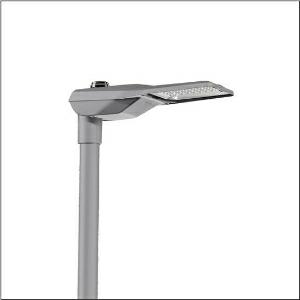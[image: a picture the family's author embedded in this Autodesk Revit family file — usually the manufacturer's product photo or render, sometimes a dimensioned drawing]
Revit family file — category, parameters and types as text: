
# Revit family: streetlight_sl_21_mini___st0_5a_5xe6b37n08hb_16a2
name_source: partatom
category: Lighting Fixtures
units: mm (PartAtom-declared; Revit-internal decimal feet)

## family parameters
Cut with Voids When Loaded = No
Host = Face
Light Source = No
Part Type = Normal
Room Calculation Point = No
Round Connector Dimension = Use Diameter
Shared = No

## types (1)
- --- (1 x LED, 9040 lm, 66 W, 3000K)
    Apparent Load = 66 VA
    CIE Flux Codes = 41 75 97 100 100
    Color Rendering = 70
    Color Temperature = 3000K
    Default Elevation = 1800 mm
    Description = Streetlight SL 21 mini, mast luminaire, primary light control with lens, of PMMA, primary optical cover: cover, of toughened safety glass, transparent, light distribution: ST0.5a, light emission: direct distribution, primary light characteristic: asymmetric, installation type: side-entry, LED, 3G 1.5mm², High Power LED, rated luminous flux: 9.040lm, luminous efficacy: 137lm/W, light colour: 730, colour temperature: 3000K, control gear: NEMA (7pin), control: overheat protection, pre-setting: linear dimming characteristic, constant luminous flux control, time-dependent luminous flux control, flexible luminous flux parameterisation, mains connection: 230..240V, AC, 50/60Hz, connection cable pre-assembled, cable length: 8,5m, wiring characteristics: H07RN-F, start of lifetime: 66W, end of service life: 69W, reduction: 30W, luminaire housing, of diecast aluminium (EN AC-44300), powder-coated, Siteco® metallic grey (DB 702S), corrosivity category C5 mid according to DIN EN ISO 12944, multi-level sealing system, sealing non-destructively replaceable, inclination adjustable: 0°, 5°, 10°, 15°, length: 628mm, width: 235mm, height: 110mm, spigot size: 42mm (side-entry), mounting height: 4..8m, protection rating (complete): IP66, insulation class (complete): insulation class I (protective earthing), certification: CE, ENEC, ENEC+, VDE, impact resistance: IK10, permissible operating ambient temperature for outdoor applications: -40..+50°C, standard-compliant lighting for roads and squares, packaging unit: 1 piece

Light Distribution: ST0.5a
    Height = 110 mm
    Lamp = 1 x LED
    Lamp Light Flux = 9040 lm
    Lamp Power = 66 W
    Lamp count = 1
    Length = 625 mm
    Luminous efficacy = 137 lm/W
    Manufacturer = Siteco
    ModVariant = No
    Model = 5XE6B37N08HB
    Number of Poles = 1
    OnlyDefault = Yes
    Power Factor = 1
    Product Name = Streetlight SL 21 mini | ST0.5a
    Product group = mast luminaire | pylon top
    ProductGroupID = 6100
    Protection Class = Protection class I
    Protection Degree = IP 66
    RLX_Detail_Level = 1
    RLX_Emergency_Light_Flux = 0 lm
    RLX_Emergency_Type = 0
    RLX_Emergency_Type_DB = No
    RlxData = <blob elided: 37149 chars, md5=a6d228c2>
    Socket = socket
    Standby Power = 0 W
    System Light Flux = 9040 lm
    System Power = 66 W
    Type Comments = factory setting: luminous flux: 100 % | dim-lin: 254 | 670 mA
    Type Image = l_1294379.jpg
    URL = http://relux.com
    VarID = @adj_158975
    Voltage = 0 V
    Weight = 0.00 kg
    Width = 234 mm

## geometry (parser evidence)
native form markers: Blend x4, Sweep x10
no freeform markers — native parametric forms only
